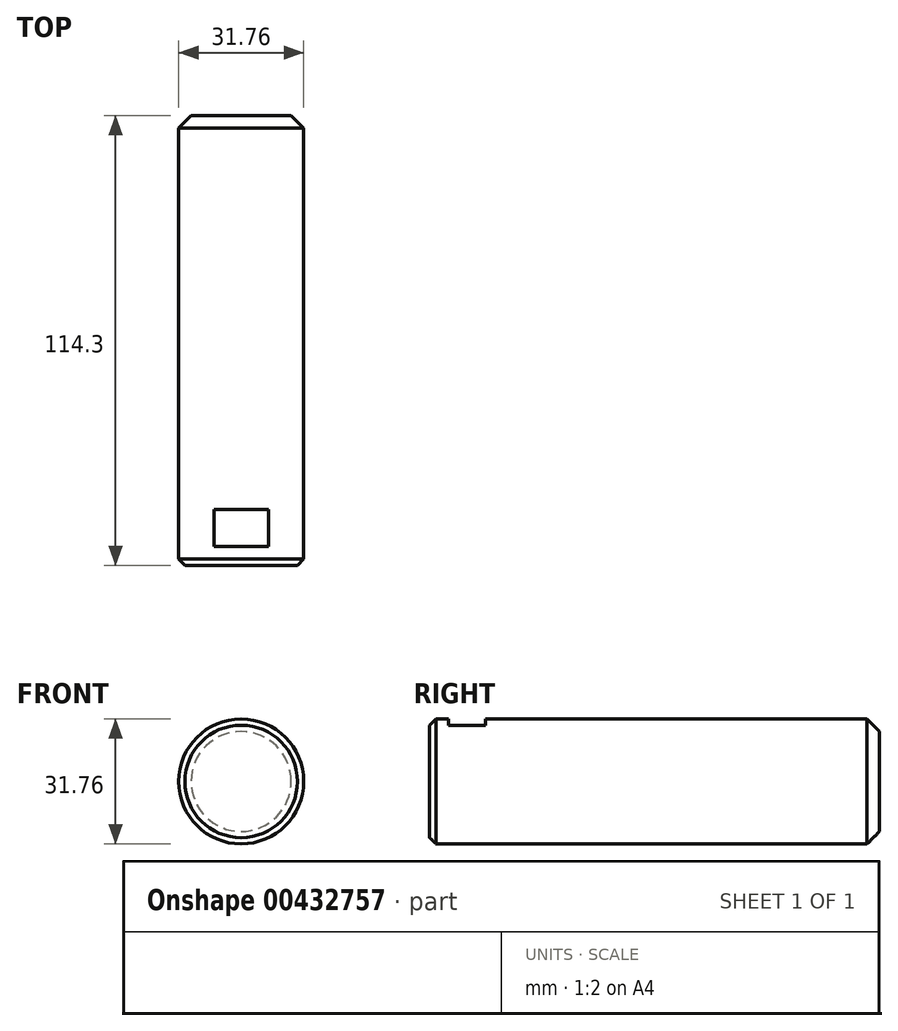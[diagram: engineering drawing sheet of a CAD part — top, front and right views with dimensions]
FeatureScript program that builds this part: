
annotation { "Feature Type Name" : "Feature", "Feature Type Description" : "" }
export const myFeature = defineFeature(function(context is Context, id is Id, definition is map)
    precondition{}
    {
        {
            var Q0;
            Q0=qCreatedBy(makeId("Front.planeOp"),FACE);
            var sketch = newSketch(context, id + "F0", { "sketchPlane" : qUnion([Q0])});
            skCircle(sketch, "E0", {"center": v(0, 0) * mm, "radius": 15.88 * mm});
            skSolve(sketch);
        }
        {
            var Q0;
            Q0=makeQuery(id+"F0.imprint","IMPRINT",FACE,{"disambiguationData":[TD([[makeQuery(id+"F0.imprint","IMPRINT",EDGE,{"derivedFrom":sQuery(id+"F0.wireOp",EDGE,"E0")}),1.0]])]});
            extrude(context, id + "F1", {"entities" : qUnion([Q0]), "depth" : 101.6 * mm, "hasSecondDirection" : true, "secondDirectionOppositeDirection" : true, "secondDirectionDepth" : 12.7 * mm});
        }
        {
            var Q0;
            Q0=makeQuery(id+"F1.opExtrude","CAP_EDGE",EDGE,{"disambiguationData":[OSD([sQuery(id+"F0.wireOp",EDGE,"E0")])],"isStart":false});
            chamfer(context, id + "F2", {"entities" : qUnion([Q0]), "width" : 1.59 * mm, "tangentPropagation" : true});
        }
        {
            var Q0;
            Q0=makeQuery(id+"F1.opExtrude","CAP_EDGE",EDGE,{"disambiguationData":[OSD([sQuery(id+"F0.wireOp",EDGE,"E0")])],"isStart":true});
            chamfer(context, id + "F3", {"entities" : qUnion([Q0]), "width" : 3.17 * mm, "tangentPropagation" : true});
        }
        {
            var Q0;
            Q0=makeQuery(id+"F1.opExtrude","CAP_FACE",FACE,{"disambiguationData":[OSD([sQuery(id+"F0.wireOp",EDGE,"E0")])],"isStart":false});
            var sketch = newSketch(context, id + "F4", { "sketchPlane" : qUnion([Q0])});
            skCircle(sketch, "E1", {"center": v(0, 0) * mm, "radius": 15.88 * mm});
            skLineSegment(sketch, "E2", {"start": v(0, 14.29) * mm, "end": v(-12.97, 14.29) * mm});
            skLineSegment(sketch, "E3", {"start": v(0, 14.29) * mm, "end": v(15.14, 14.29) * mm});
            skSolve(sketch);
        }
        {
            var Q0;
            {var subQ0=sQuery(id+"F4.wireOp",EDGE,"E2");var subQ1=sQuery(id+"F4.wireOp",EDGE,"E1");var subQ2=makeQuery(id+"F4.imprint","INTERSECT",VERTEX,{"derivedFrom":[subQ1,subQ0]});Q0=makeQuery(id+"F4.imprint","IMPRINT",FACE,{"disambiguationData":[TD([[makeQuery(id+"F4.imprint","IMPRINT",EDGE,{"disambiguationData":[TD([[subQ2,1.0]])],"derivedFrom":subQ1}),1.0]])]});}
            var Q1;
            Q1=sQuery(id+"F4.wireOp",EDGE,"E3");
            var Q2;
            Q2=sQuery(id+"F4.wireOp",EDGE,"E2");
            extrude(context, id + "F5", {"entities" : qUnion([Q0]), "operationType" : NewBodyOperationType.REMOVE, "surfaceEntities" : qUnion([Q1, Q2]), "oppositeDirection" : true, "depth" : 14.21 * mm, "hasSecondDirection" : true, "secondDirectionOppositeDirection" : true, "secondDirectionDepth" : 4.76 * mm});
        }
    });
